# Revit family: 3-635-xx - 37-635-xx - Idol (Pendant)
name_source: partatom
category: Lighting Fixtures
revit_build: Autodesk Revit 2018 (Build: 20170223_1515(x64)
units: mm (PartAtom-declared; Revit-internal decimal feet)

## family parameters
Always vertical = Yes
Cut with Voids When Loaded = No
Host = Ceiling
Light Source = Yes
OmniClass Number = 23.80.70.11
OmniClass Title = Luminaries for Internal Lighting
Part Type = Normal
Room Calculation Point = No
Round Connector Dimension = Use Diameter
Shared = No

## types (3) — shared parameters
Color Filter = 16777215
Diffuser = Oxygen Lighting - Diffuser - Matte White Acrylic
Dimming Lamp Color Temperature Shift = <None>
Emit Shape Visible in Rendering = No
Emit from Circle Diameter = 5 "
Keynote = LED array lamp
Lamp = LED Array
Manufacturer = Oxygen Lighting
Model = 3-635-xx / 37-635-xx - Idol
Others = Rubber
Photometric Web File = 3-635 Idol Pendant.ies
Tilt Angle = 90.00°
Type Comments = LED Lighting Fixture
URL = www.oxygenlighting.com
Wattage Comments = 6.64 W at 120 V
zero-valued in all types: Cost

## per-type parameters (varying)
| type | Metal Finish |
| 3-635-14 / 37-635-14 - Idol | Oxygen Lighting - Metal Finish - 14 - Polished Chrome |
| 3-635-18 / 37-635-18 - Idol | Oxygen Lighting - Metal Finish - 18 - Gunmetal |
| 3-635-24 / 37-635-24 - Idol | Oxygen Lighting - Metal Finish - 24 - Satin Nickel |

## geometry (parser evidence)
native form markers: Sweep x10
no freeform markers — native parametric forms only
